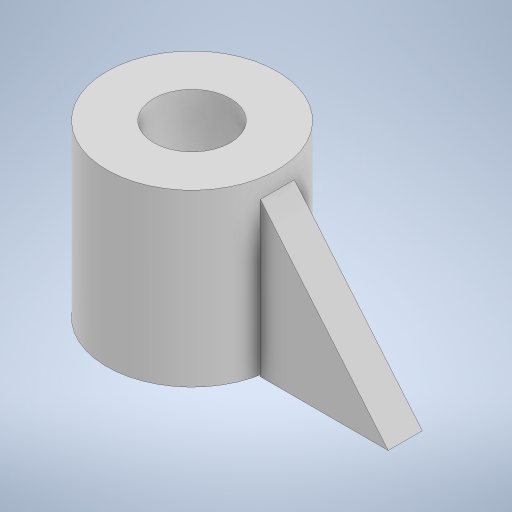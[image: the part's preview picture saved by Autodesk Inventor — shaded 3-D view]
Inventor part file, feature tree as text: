
AUTODESK INVENTOR PART (.ipt)
format: ipt  version: 2023.2 (Build 272271030, 271C)  size: 224,768 bytes
history: native  units: mm
features: extrude x3, sketch x2, projected_geometry x1
ambient origin geometry x8: Origin, YZ Plane, XZ Plane, XY Plane, X Axis, Y Axis, Z Axis, Center Point
bodies: Solid1 (feature_tree)
feature tree (6):
  sketch  "Sketch1"  dims[d0=9.0mm d1=20.0mm]
  extrude  "Extrusion1"  Depth=20.0mm
  extrude  "Extrusion2"  Depth=16.0mm TaperAngle=0.0deg
  extrude  "Extrusion3"  Depth=4.0mm
  sketch  "Sketch2"  dims[d2=20.0mm d3=0.0mm d4=16.0mm d5=0.0mm d6=15.0mm d7=18.0mm d8=4.0mm d9=0.0mm]
  projected_geometry  "Projected Loop1"
